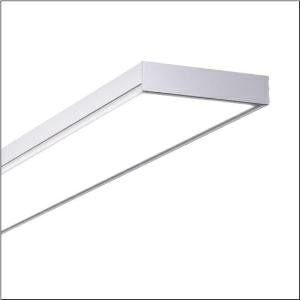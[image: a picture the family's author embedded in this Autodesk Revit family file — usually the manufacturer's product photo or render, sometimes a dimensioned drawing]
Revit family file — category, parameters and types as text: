
# Revit family: apollon_31_surface_51mp25wm2441ea
name_source: partatom
category: Lighting Fixtures
units: mm (PartAtom-declared; Revit-internal decimal feet)

## family parameters
Cut with Voids When Loaded = No
Host = Face
Light Source = No
Part Type = Normal
Room Calculation Point = No
Round Connector Dimension = Use Diameter
Shared = No

## types (1)
- Apollon 31 Surface (1 x LED, 3800 lm, 27 W, 4000K)
    Apparent Load = 27 VA
    CIE Flux Codes = 61 87 97 97 100
    Color Rendering = 80
    Color Temperature = 4000K
    Default Elevation = 1800 mm
    Description = Apollon 31 Surface, office luminaire, primary optical cover: micro prismatic cover, of PMMA, light emission: direct distribution, primary light characteristic: symmetric, installation type: surface-mounted, LED, rated luminous flux: 3.800lm, luminous efficacy: 139lm/W, light colour: 840, colour temperature: 4000K, control gear: ON/OFF Multilumen, with terminal, 3-pole, mains connection: 220..240V, AC, 50/60Hz, rated input power: 27W, housing, of sheet steel, coated, metallic grey (RAL 9006), length: 1.245mm, width: 200mm, height: 44mm, protection rating (complete): IP20, protection rating (on room side): IP40, protection rating (lamp compartment, on room side): IP40, insulation class (complete): insulation class I (protective earthing), certification: CE, ENEC, UKCA, impact resistance: IK02, permissible operating ambient temperature: -20..+40°C, packaging unit: 1 piece
    Height = 44 mm
    Lamp = 1 x LED
    Lamp Light Flux = 3800 lm
    Lamp Power = 27 W
    Lamp count = 1
    Length = 1245 mm
    Luminous efficacy = 141 lm/W
    Manufacturer = Siteco
    ModVariant = No
    Model = 51MP25WM2441EA
    Mounting Place = Ceiling
    Mounting Type = Surface mounted
    Number of Poles = 1
    OnlyDefault = Yes
    Power Factor = 1
    Product Name = Apollon 31 Surface
    Product group = office luminaire | ceiling mounted
    ProductGroupID = 301
    Protection Class = Protection class I
    Protection Degree = IP 20
    RLX_Detail_Level = 1
    RLX_Emergency_Light_Flux = 0 lm
    RLX_Emergency_Type = 0
    RLX_Emergency_Type_DB = No
    RlxData = <blob elided: 24133 chars, md5=da45e19f>
    Socket = socket
    Standby Power = 0 W
    System Light Flux = 3800 lm
    System Power = 27 W
    Type Comments = Product without accessories
    Type Image = l_1313654.jpg
    URL = http://relux.com
    VarID = ---
    Voltage = 0 V
    Weight = 0.00 kg
    Width = 200 mm  [stored 0.656168 ft]

note: [stored X ft] marks values corroborated as IEEE doubles in the binary element streams (Revit-internal decimal feet)

## geometry (parser evidence)
native form markers: Blend x4, Sweep x9
no freeform markers — native parametric forms only
